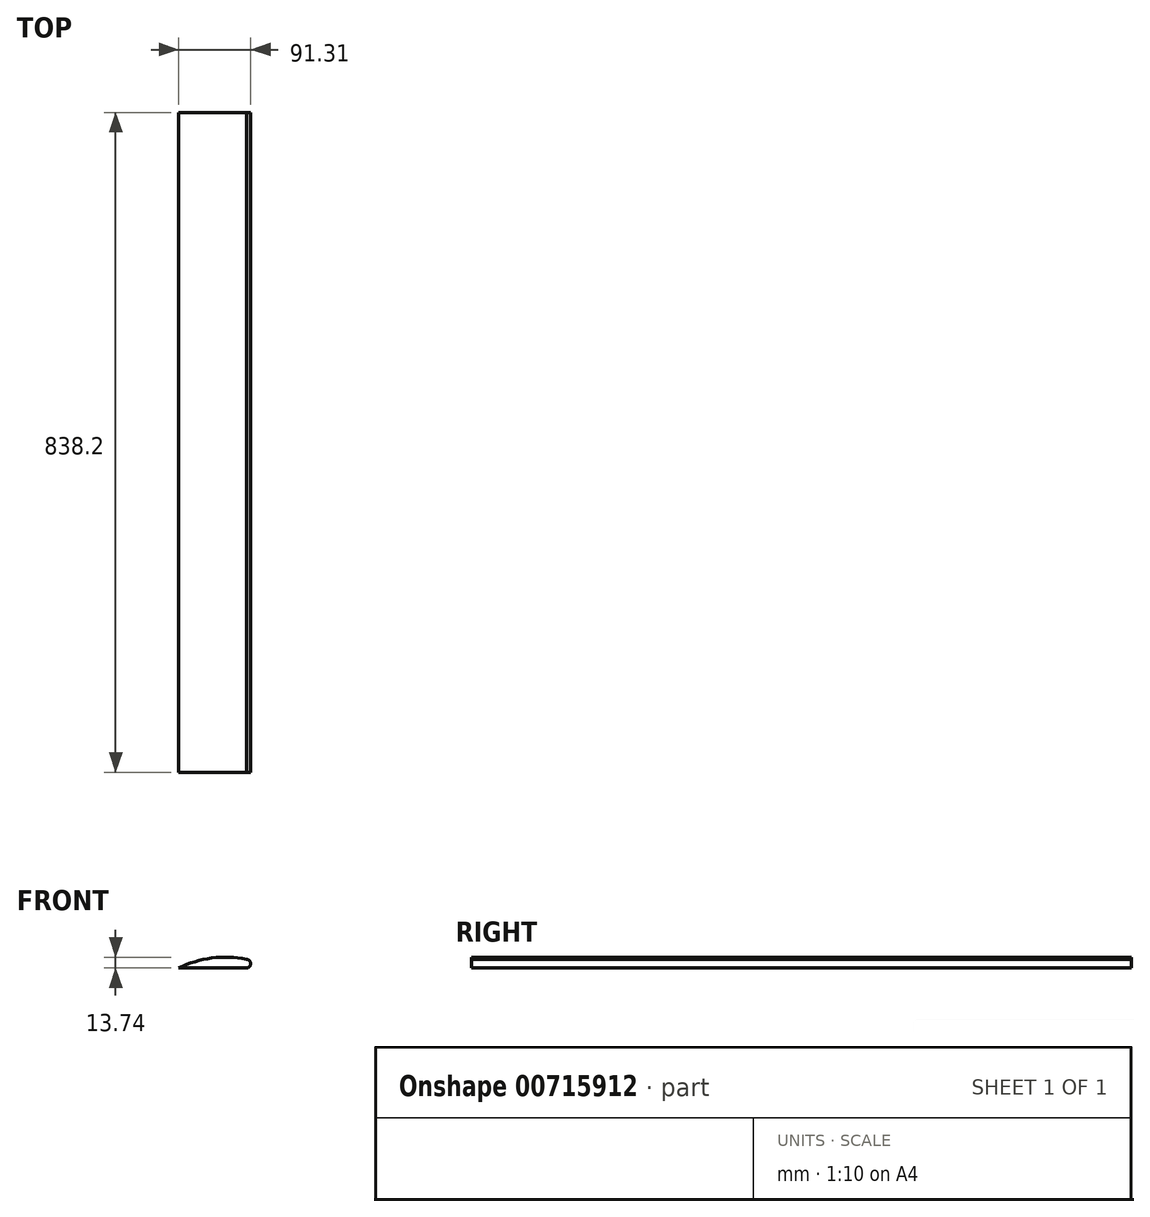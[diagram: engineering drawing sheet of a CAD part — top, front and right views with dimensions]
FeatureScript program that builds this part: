
annotation { "Feature Type Name" : "Feature", "Feature Type Description" : "" }
export const myFeature = defineFeature(function(context is Context, id is Id, definition is map)
    precondition{}
    {
        {
            var Q0;
            Q0=qCreatedBy(makeId("Front.planeOp"),FACE);
            var sketch = newSketch(context, id + "F0", { "sketchPlane" : qUnion([Q0])});
            skLineSegment(sketch, "E0", {"start": v(0, 0) * mm, "end": v(-71.37, 0) * mm});
            skCircle(sketch, "E1", {"center": v(0, 0) * mm, "radius": 5.52 * mm});
            skLineSegment(sketch, "E2", {"start": v(0, -5.52) * mm, "end": v(-85.79, -5.52) * mm});
            skArc(sketch, "E3", {"start": v(0, 5.52) * mm, "mid": v(-43.81, 7.13) * mm, "end": v(-85.79, -5.52) * mm});
            skSolve(sketch);
        }
        {
            var Q0;
            {var subQ3=sQuery(id+"F0.wireOp",EDGE,"E2");Q0=makeQuery(id+"F0.imprint","IMPRINT",FACE,{"disambiguationData":[TD([[makeQuery(id+"F0.imprint","IMPRINT",EDGE,{"derivedFrom":subQ3}),-1.0]])]});}
            var Q1;
            {var subQ0=sQuery(id+"F0.wireOp",EDGE,"E1");var subQ2=makeQuery(id+"F0.imprint","IMPRINT",VERTEX,{"derivedFrom":subQ0});Q1=makeQuery(id+"F0.imprint","IMPRINT",FACE,{"disambiguationData":[TD([[makeQuery(id+"F0.imprint","IMPRINT",EDGE,{"disambiguationData":[TD([[subQ2,1.0]])],"derivedFrom":subQ0}),1.0]])]});}
            var Q2;
            Q2=sQuery(id+"F0.wireOp",EDGE,"E1");
            var Q3;
            Q3=sQuery(id+"F0.wireOp",EDGE,"E3");
            var Q4;
            Q4=sQuery(id+"F0.wireOp",EDGE,"E2");
            extrude(context, id + "F1", {"entities" : qUnion([Q0, Q1]), "surfaceOperationType" : NewSurfaceOperationType.ADD, "surfaceEntities" : qUnion([Q2, Q3, Q4]), "depth" : 838.2 * mm, "offsetDistance" : 25.4 * mm});
        }
    });
